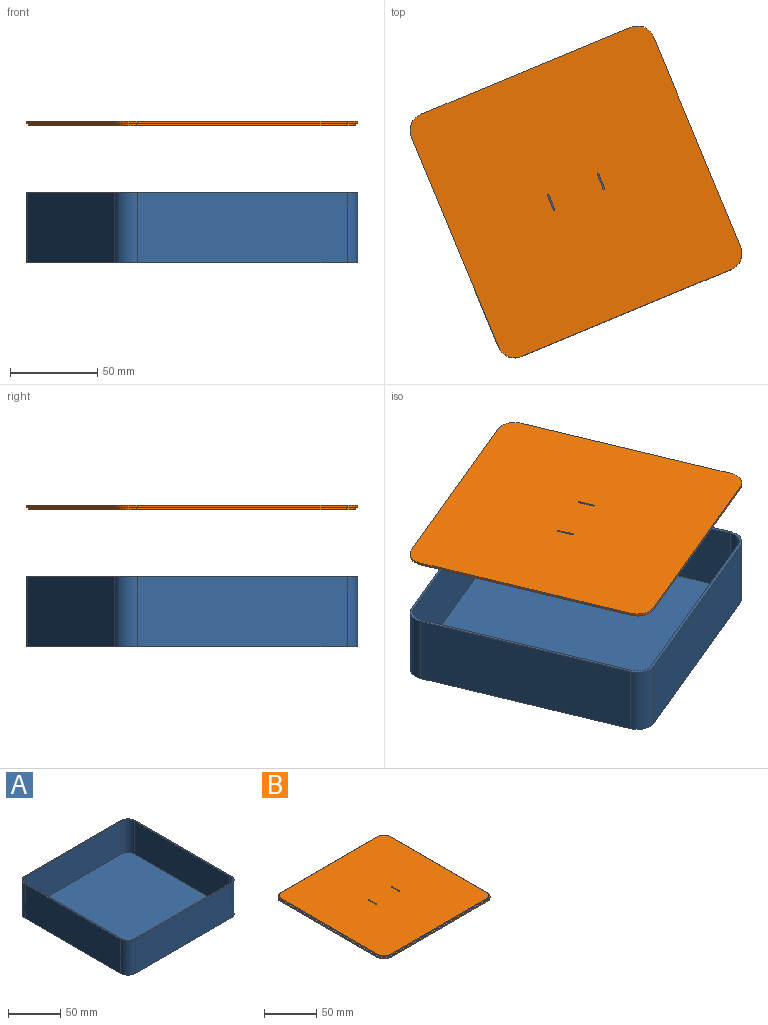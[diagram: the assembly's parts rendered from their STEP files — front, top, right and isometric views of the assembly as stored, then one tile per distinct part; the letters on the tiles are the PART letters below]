
ASSEMBLY  parts=2 mates=1
PART A: 19 faces, bbox 150x150x40 mm
  f0: plane 150x150mm, normal (0,0,1), area 867.2mm2, adj f1,f2,f3,f4,f5,f6,f7,f8
  f1: plane 130x40mm, normal (-1,0,0), area 5200mm2, adj f0,f2,f8,f9
  f2: cylinder r=10mm len=40mm, axis (0,0,-1), area 628.3mm2, adj f0,f1,f3,f9
  f3: plane 130x40mm, normal (0,-1,0), area 5200mm2, adj f0,f2,f4,f9
  f4: cylinder r=10mm len=40mm, axis (0,0,-1), area 628.3mm2, adj f0,f3,f5,f9
  f5: plane 130x40mm, normal (1,0,0), area 5200mm2, adj f0,f4,f6,f9
  f6: cylinder r=10mm len=40mm, axis (0,0,-1), area 628.3mm2, adj f0,f5,f7,f9
  f7: plane 130x40mm, normal (0,1,0), area 5200mm2, adj f0,f6,f8,f9
  f8: cylinder r=10mm len=40mm, axis (0,0,-1), area 628.3mm2, adj f0,f1,f7,f9
  f9: plane 150x150mm, normal (0,0,-1), area 22414.2mm2, adj f1,f2,f3,f4,f5,f6,f7,f8
  f10: plane 130x38.5mm, normal (1,0,0), area 5005mm2, adj f0,f11,f17,f18
  f11: cylinder r=8.5mm len=38.5mm, axis (0,0,-1), area 514mm2, adj f0,f10,f12,f18
  f12: plane 130x38.5mm, normal (0,1,0), area 5005mm2, adj f0,f11,f13,f18
  f13: cylinder r=8.5mm len=38.5mm, axis (0,0,-1), area 514mm2, adj f0,f12,f14,f18
  f14: plane 130x38.5mm, normal (-1,0,0), area 5005mm2, adj f0,f13,f15,f18
  f15: cylinder r=8.5mm len=38.5mm, axis (0,0,-1), area 514mm2, adj f0,f14,f16,f18
  f16: plane 130x38.5mm, normal (0,-1,0), area 5005mm2, adj f0,f15,f17,f18
  f17: cylinder r=8.5mm len=38.5mm, axis (0,0,-1), area 514mm2, adj f0,f10,f16,f18
  f18: plane 147x147mm, normal (0,0,1), area 21547mm2, adj f10,f11,f12,f13,f14,f15,f16,f17
PART B: 27 faces, bbox 150x150x2.5 mm
  f0: plane 150x150mm, normal (0,0,-1), area 22394.6mm2, adj f3,f4,f5,f6,f7,f8,f9,f10
  f1: plane 147x147mm, normal (0,0,1), area 21527.4mm2, adj f11,f12,f13,f14,f15,f16,f17,f18
  f2: plane 150x150mm, normal (0,0,1), area 867.2mm2, adj f3,f4,f5,f6,f7,f8,f9,f10
  f3: plane 130x1.25mm, normal (-1,0,0), area 162.5mm2, adj f0,f2,f4,f10
  f4: cylinder r=10mm len=10mm, axis (0,0,-1), area 19.6mm2, adj f0,f2,f3,f5
  f5: plane 130x1.25mm, normal (0,-1,0), area 162.5mm2, adj f0,f2,f4,f6
  f6: cylinder r=10mm len=10mm, axis (0,0,-1), area 19.6mm2, adj f0,f2,f5,f7
  f7: plane 130x1.25mm, normal (1,0,0), area 162.5mm2, adj f0,f2,f6,f8
  f8: cylinder r=10mm len=10mm, axis (0,0,-1), area 19.6mm2, adj f0,f2,f7,f9
  f9: plane 130x1.25mm, normal (0,1,0), area 162.5mm2, adj f0,f2,f8,f10
  f10: cylinder r=10mm len=10mm, axis (0,0,-1), area 19.6mm2, adj f0,f2,f3,f9
  f11: plane 130x1.25mm, normal (-1,0,0), area 162.5mm2, adj f1,f2,f12,f18
  f12: cylinder r=8.5mm len=8.5mm, axis (0,0,-1), area 16.7mm2, adj f1,f2,f11,f13
  f13: plane 130x1.25mm, normal (0,-1,0), area 162.5mm2, adj f1,f2,f12,f14
  f14: cylinder r=8.5mm len=8.5mm, axis (0,0,-1), area 16.7mm2, adj f1,f2,f13,f15
  f15: plane 130x1.25mm, normal (1,0,0), area 162.5mm2, adj f1,f2,f14,f16
  f16: cylinder r=8.5mm len=8.5mm, axis (0,0,-1), area 16.7mm2, adj f1,f2,f15,f17
  f17: plane 130x1.25mm, normal (0,1,0), area 162.5mm2, adj f1,f2,f16,f18
  f18: cylinder r=8.5mm len=8.5mm, axis (0,0,-1), area 16.7mm2, adj f1,f2,f11,f17
  f19: plane 9x2.5mm, normal (1,0,0), area 22.5mm2, adj f0,f1,f23,f24
  f20: plane 9x2.5mm, normal (-1,0,0), area 22.5mm2, adj f0,f1,f23,f24
  f21: plane 9x2.5mm, normal (-1,0,0), area 22.5mm2, adj f0,f1,f25,f26
  f22: plane 9x2.5mm, normal (1,0,0), area 22.5mm2, adj f0,f1,f25,f26
  f23: cylinder r=0.5mm len=2.5mm, axis (0,0,-1), area 3.9mm2, adj f0,f1,f19,f20
  f24: cylinder r=0.5mm len=2.5mm, axis (0,0,1), area 3.9mm2, adj f0,f1,f19,f20
  f25: cylinder r=0.5mm len=2.5mm, axis (0,0,1), area 3.9mm2, adj f0,f1,f21,f22
  f26: cylinder r=0.5mm len=2.5mm, axis (0,0,-1), area 3.9mm2, adj f0,f1,f21,f22
PLACE A rot(axis=(0,0,-1),157.5deg) t=(-131.55,95.22,-25.73)mm
PLACE B rot(axis=(-0.98,-0.2,0),180deg) t=(-129.11,100.8,55.21)mm
MATE slider A.f8 <-> B.f8  axis (0,0,-1) through (-46.61,60.08,14.27)mm
